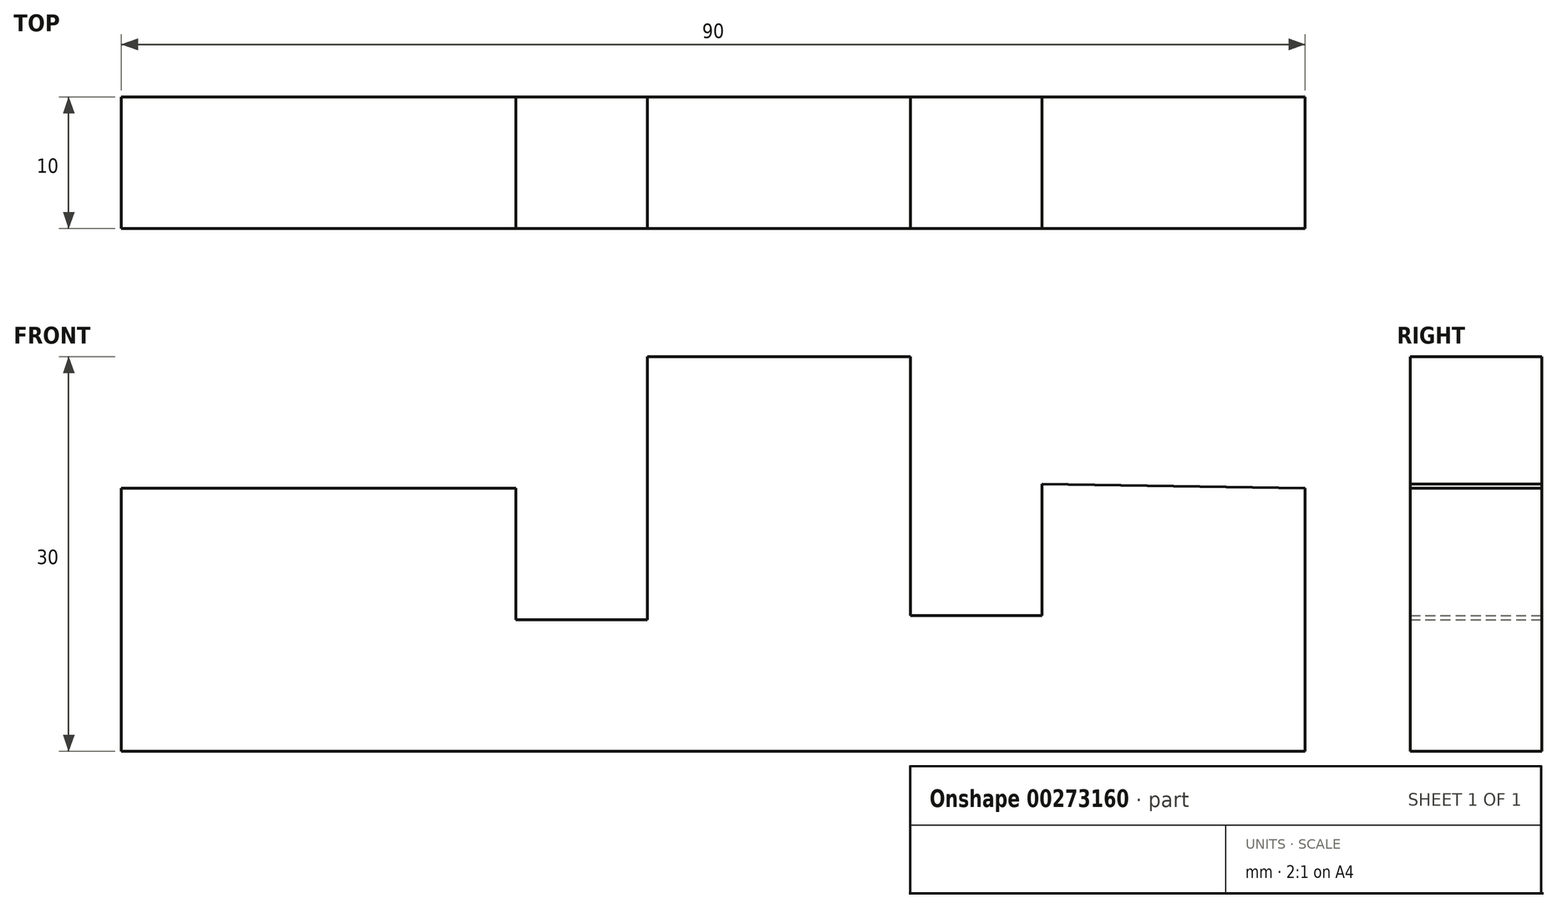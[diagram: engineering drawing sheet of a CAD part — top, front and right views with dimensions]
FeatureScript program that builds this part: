
annotation { "Feature Type Name" : "Feature", "Feature Type Description" : "" }
export const myFeature = defineFeature(function(context is Context, id is Id, definition is map)
    precondition{}
    {
        {
            var Q0;
            Q0=qCreatedBy(makeId("Front.planeOp"),FACE);
            var sketch = newSketch(context, id + "F0", { "sketchPlane" : qUnion([Q0])});
            skLineSegment(sketch, "E0", {"start": v(0, 0) * mm, "end": v(90, 0) * mm});
            skLineSegment(sketch, "E1", {"start": v(0, 0) * mm, "end": v(0, 20) * mm});
            skLineSegment(sketch, "E2", {"start": v(90, 0) * mm, "end": v(90, 20) * mm});
            skLineSegment(sketch, "E3", {"start": v(0, 20) * mm, "end": v(30, 20) * mm});
            skLineSegment(sketch, "E4", {"start": v(30, 20) * mm, "end": v(30, 10) * mm});
            skLineSegment(sketch, "E5", {"start": v(30, 10) * mm, "end": v(40, 10) * mm});
            skLineSegment(sketch, "E6", {"start": v(40, 10) * mm, "end": v(40, 30) * mm});
            skLineSegment(sketch, "E7", {"start": v(40, 30) * mm, "end": v(60, 30) * mm});
            skLineSegment(sketch, "E8", {"start": v(60, 30) * mm, "end": v(60, 10.33) * mm});
            skLineSegment(sketch, "E9", {"start": v(60, 10.33) * mm, "end": v(70, 10.33) * mm});
            skLineSegment(sketch, "E10", {"start": v(70, 10.33) * mm, "end": v(70, 20.33) * mm});
            skLineSegment(sketch, "E11", {"start": v(70, 20.33) * mm, "end": v(90, 20) * mm});
            skSolve(sketch);
        }
        {
            var Q0;
            Q0 = qSketchRegion(id + "F0", true);
            extrude(context, id + "F1", {"entities" : qUnion([Q0]), "depth" : 10 * mm});
        }
    });
